# Revit family: Олимп_Скамейка
name_source: partatom
category: Мебель
revit_build: Autodesk Revit 2017 (Build: 20160225_1515(x64)
units: mm (PartAtom-declared; Revit-internal decimal feet)

## family parameters
Всегда вертикально = Да
Заголовок OmniClass = General Furniture and Specialties
На основе рабочей плоскости = Нет
Номер OmniClass = 23.40.20.00
Общий = Нет
При загрузке вырезать с полостями = Нет
Точка расчета площади = Нет

## types (1)
- Рекламная скамейка «Олимп» 1,5м
    ADSK_Код изделия = 6903
    ADSK_Материал доски = <По категории>
    ADSK_Материал опоры = <По категории>
    ADSK_Материал рекламного щита = <По категории>
    ADSK_Материал фурнитуры = <По категории>
    ADSK_Наименование = Рекламная скамейка «Олимп»
    ADSK_Размер_Высота = 970 мм
    ADSK_Размер_Высота сидения = 440 мм
    ADSK_Размер_Длина = 1500 мм
    ADSK_Размер_Ширина = 670 мм
    ADSK_Размер_Ширина сидения = 420 мм
    URL = https://hobbyka.ru
    Длина доски = 1486 мм
    Длина доски на спинке = 1486 мм
    Изготовитель = ООО "Хоббика"
    Перемычка = Да
    Стоимость = 12400 $
